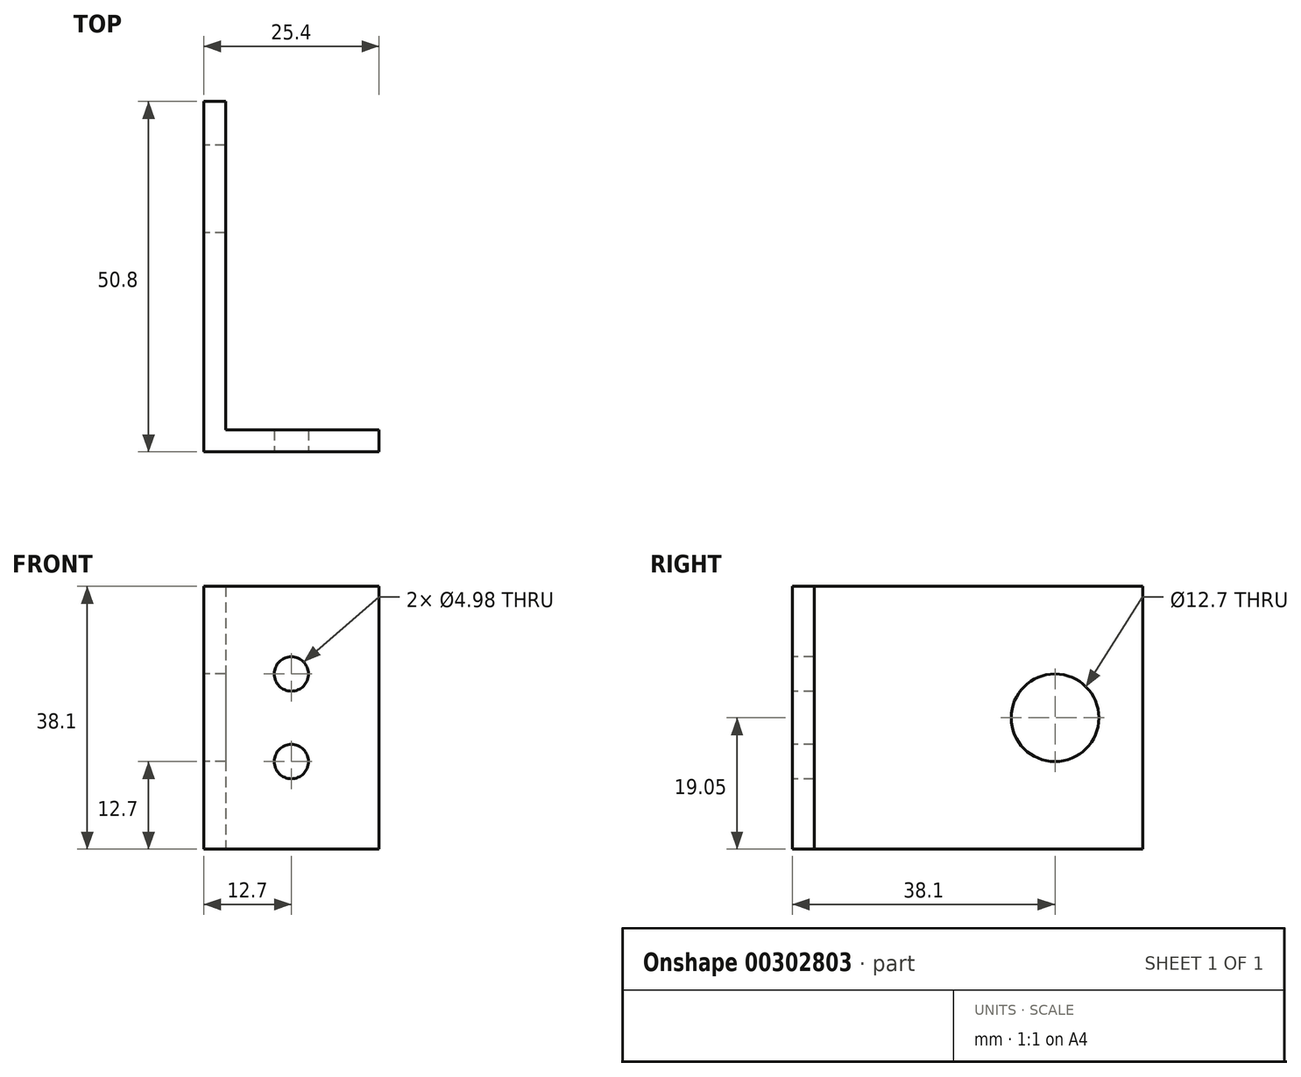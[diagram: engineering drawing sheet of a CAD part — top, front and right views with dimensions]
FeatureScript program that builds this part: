
annotation { "Feature Type Name" : "Feature", "Feature Type Description" : "" }
export const myFeature = defineFeature(function(context is Context, id is Id, definition is map)
    precondition{}
    {
        {
            var Q0;
            Q0=qCreatedBy(makeId("Top.planeOp"),FACE);
            var sketch = newSketch(context, id + "F0", { "sketchPlane" : qUnion([Q0])});
            skLineSegment(sketch, "E0", {"start": v(0, 50.8) * mm, "end": v(0, 0) * mm});
            skLineSegment(sketch, "E1", {"start": v(0, 0) * mm, "end": v(25.4, 0) * mm});
            skLineSegment(sketch, "E2", {"start": v(25.4, 0) * mm, "end": v(25.4, 3.18) * mm});
            skLineSegment(sketch, "E3", {"start": v(25.4, 3.18) * mm, "end": v(3.17, 3.18) * mm});
            skLineSegment(sketch, "E4", {"start": v(3.17, 3.18) * mm, "end": v(3.17, 50.8) * mm});
            skLineSegment(sketch, "E5", {"start": v(3.17, 50.8) * mm, "end": v(0, 50.8) * mm});
            skSolve(sketch);
        }
        {
            var Q0;
            Q0 = qSketchRegion(id + "F0", true);
            extrude(context, id + "F1", {"entities" : qUnion([Q0]), "depth" : 38.1 * mm});
        }
        {
            var Q0;
            Q0=makeQuery(id+"F1.opExtrude","SWEPT_FACE",FACE,{"disambiguationData":[OSD([sQuery(id+"F0.wireOp",EDGE,"E1")])]});
            var sketch = newSketch(context, id + "F2", { "sketchPlane" : qUnion([Q0])});
            skCircle(sketch, "E6", {"center": v(12.7, 25.4) * mm, "radius": 2.49 * mm});
            skCircle(sketch, "E7", {"center": v(12.7, 12.7) * mm, "radius": 2.49 * mm});
            skSolve(sketch);
        }
        {
            var Q0;
            Q0 = qSketchRegion(id + "F2", true);
            extrude(context, id + "F3", {"entities" : qUnion([Q0]), "operationType" : NewBodyOperationType.REMOVE, "endBound" : BoundingType.THROUGH_ALL, "oppositeDirection" : true, "depth" : 25.4 * mm});
        }
        {
            var Q0;
            Q0=makeQuery(id+"F1.opExtrude","SWEPT_FACE",FACE,{"disambiguationData":[OSD([sQuery(id+"F0.wireOp",EDGE,"E0")])]});
            var sketch = newSketch(context, id + "F4", { "sketchPlane" : qUnion([Q0])});
            skCircle(sketch, "E8", {"center": v(-38.1, 19.05) * mm, "radius": 6.35 * mm});
            skSolve(sketch);
        }
        {
            var Q0;
            Q0 = qSketchRegion(id + "F4", true);
            extrude(context, id + "F5", {"entities" : qUnion([Q0]), "operationType" : NewBodyOperationType.REMOVE, "endBound" : BoundingType.THROUGH_ALL, "oppositeDirection" : true, "depth" : 25.4 * mm});
        }
    });
